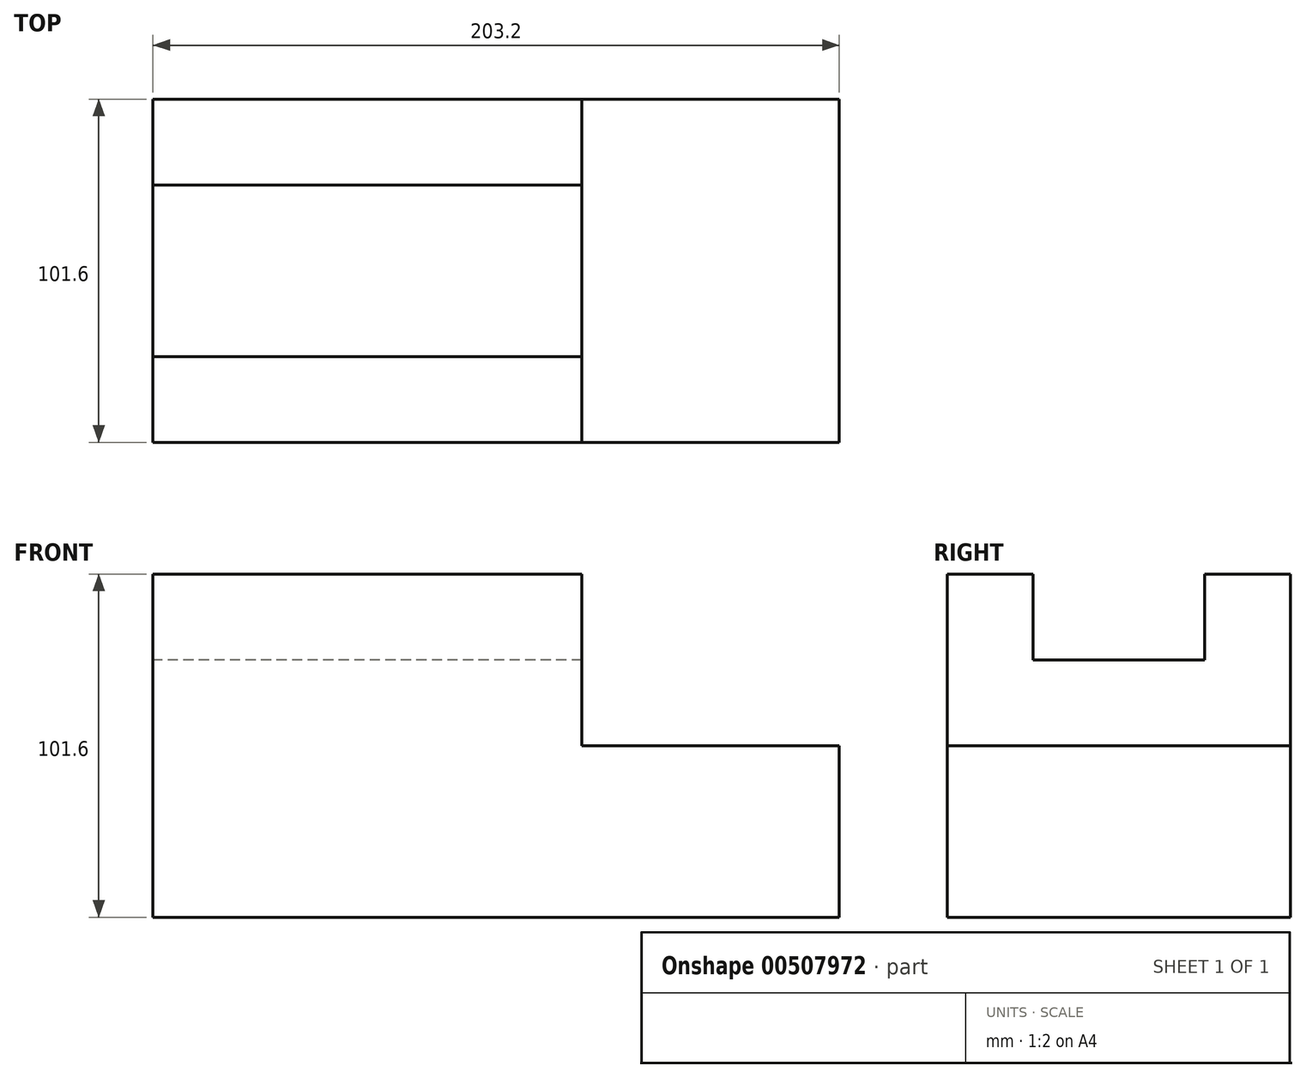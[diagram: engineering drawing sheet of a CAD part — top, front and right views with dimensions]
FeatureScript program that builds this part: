
annotation { "Feature Type Name" : "Feature", "Feature Type Description" : "" }
export const myFeature = defineFeature(function(context is Context, id is Id, definition is map)
    precondition{}
    {
        {
            var Q0;
            Q0=qCreatedBy(makeId("Front.planeOp"),FACE);
            var sketch = newSketch(context, id + "F0", { "sketchPlane" : qUnion([Q0])});
            skLineSegment(sketch, "E0.bottom", {"start": v(-101.6, 25.4) * mm, "end": v(101.6, 25.4) * mm});
            skLineSegment(sketch, "E0.top", {"start": v(-101.6, -25.4) * mm, "end": v(101.6, -25.4) * mm});
            skLineSegment(sketch, "E0.left", {"start": v(-101.6, 25.4) * mm, "end": v(-101.6, -25.4) * mm});
            skLineSegment(sketch, "E0.right", {"start": v(101.6, 25.4) * mm, "end": v(101.6, -25.4) * mm});
            skPoint(sketch, "E0.middle", {"position": v(0, 0) * mm});
            skSolve(sketch);
        }
        {
            var Q0;
            Q0=makeQuery(id+"F0.imprint","IMPRINT",FACE,{"disambiguationData":[TD([[makeQuery(id+"F0.imprint","IMPRINT",EDGE,{"derivedFrom":sQuery(id+"F0.wireOp",EDGE,"E0.bottom")}),-1.0]])]});
            extrude(context, id + "F1", {"entities" : qUnion([Q0]), "depth" : 101.6 * mm});
        }
        {
            var Q0;
            Q0=makeQuery(id+"F1.opExtrude","SWEPT_FACE",FACE,{"disambiguationData":[OSD([sQuery(id+"F0.wireOp",EDGE,"E0.left")])]});
            var sketch = newSketch(context, id + "F2", { "sketchPlane" : qUnion([Q0])});
            skLineSegment(sketch, "E1.bottom", {"start": v(0, -25.4) * mm, "end": v(25.4, -25.4) * mm});
            skLineSegment(sketch, "E1.top", {"start": v(0, 76.2) * mm, "end": v(25.4, 76.2) * mm});
            skLineSegment(sketch, "E1.left", {"start": v(0, -25.4) * mm, "end": v(0, 76.2) * mm});
            skLineSegment(sketch, "E1.right", {"start": v(25.4, -25.4) * mm, "end": v(25.4, 76.2) * mm});
            skLineSegment(sketch, "E2.bottom", {"start": v(25.4, -25.4) * mm, "end": v(76.2, -25.4) * mm});
            skLineSegment(sketch, "E2.top", {"start": v(25.4, 50.8) * mm, "end": v(76.2, 50.8) * mm});
            skLineSegment(sketch, "E2.left", {"start": v(25.4, -25.4) * mm, "end": v(25.4, 50.8) * mm});
            skLineSegment(sketch, "E2.right", {"start": v(76.2, -25.4) * mm, "end": v(76.2, 50.8) * mm});
            skLineSegment(sketch, "E3.bottom", {"start": v(76.2, -25.4) * mm, "end": v(101.6, -25.4) * mm});
            skLineSegment(sketch, "E3.top", {"start": v(76.2, 76.2) * mm, "end": v(101.6, 76.2) * mm});
            skLineSegment(sketch, "E3.left", {"start": v(76.2, -25.4) * mm, "end": v(76.2, 76.2) * mm});
            skLineSegment(sketch, "E3.right", {"start": v(101.6, -25.4) * mm, "end": v(101.6, 76.2) * mm});
            skSolve(sketch);
        }
        {
            var Q0;
            {var subQ6=sQuery(id+"F2.wireOp",EDGE,"E1.top");Q0=makeQuery(id+"F2.imprint","IMPRINT",FACE,{"disambiguationData":[TD([[makeQuery(id+"F2.imprint","IMPRINT",EDGE,{"derivedFrom":subQ6}),-1.0]])]});}
            var Q1;
            {var subQ0=sQuery(id+"F2.wireOp",EDGE,"E2.top");Q1=makeQuery(id+"F2.imprint","IMPRINT",FACE,{"disambiguationData":[TD([[makeQuery(id+"F2.imprint","IMPRINT",EDGE,{"derivedFrom":subQ0}),-1.0]])]});}
            var Q2;
            {var subQ2=sQuery(id+"F2.wireOp",EDGE,"E3.top");Q2=makeQuery(id+"F2.imprint","IMPRINT",FACE,{"disambiguationData":[TD([[makeQuery(id+"F2.imprint","IMPRINT",EDGE,{"derivedFrom":subQ2}),-1.0]])]});}
            extrude(context, id + "F3", {"entities" : qUnion([Q0, Q1, Q2]), "operationType" : NewBodyOperationType.ADD, "oppositeDirection" : true, "depth" : 127 * mm});
        }
    });
